# Revit family: 303_R401PX_+R460
name_source: partatom
category: Pipe Accessories
revit_build: Autodesk Revit 2018 (Build: 20170223_1515(x64)
units: mm (PartAtom-declared; Revit-internal decimal feet)

## family parameters
Always vertical = Yes
Cut with Voids When Loaded = No
Part Type = Valve - Breaks Into
Round Connector Dimension = Use Diameter
Shared = No
Work Plane-Based = No

## types (3) — shared parameters
CAT0 = Yes
CAT1 = No
Description = Angle valve with precision adjustment numberscale and protection cap
H4 = 2 mm  [stored 0.00656168 ft]
J1 = 6 mm  [stored 0.019685 ft]
J2 = 2 mm  [stored 0.00656168 ft]
J4 = 6 mm  [stored 0.019685 ft]
J5 = 6 mm  [stored 0.019685 ft]
L2D_Min = 3048 mm
M1 = 12 mm  [stored 0.0393701 ft]
M3 = 17 mm
M3__ve = -17 mm
Manufacturer = Giacomini
QmdConnectorList = 301;D;302;D1
TR1 = 15 mm  [stored 0.0492126 ft]
URL = http://www.giacomini.com
X1 = 17 mm
magiPartTypeId = 303
magiProductFamilyId = R401PX*+R460
zero-valued in all types: MC_Default_elevation

## per-type parameters (varying)
- R401PX032+R460: B1=6 mm  [stored 0.019685 ft]; B4=9 mm  [stored 0.0295276 ft]; CenSd_K1_6=10 mm  [stored 0.0328084 ft]; CenSd_W2_6=12 mm  [stored 0.0393701 ft]; D=10 mm; D1=10 mm; G1=5 mm  [stored 0.0164042 ft]; G3=7 mm  [stored 0.0229659 ft]; H3=4 mm  [stored 0.0131234 ft]; H3__ve=-4 mm; J=22 mm  [stored 0.0721785 ft]; K1=11 mm  [stored 0.0360892 ft]; KH=11 mm  [stored 0.0360892 ft]; KH__ve=-11 mm  [stored -0.0360892 ft]; L=40 mm  [stored 0.131234 ft]; L1=8 mm  [stored 0.0262467 ft]; L1__ve=-8 mm; L2D=40 mm  [stored 0.131234 ft]; LX=53 mm; R1=5 mm  [stored 0.0164042 ft]; TH2=78 mm; W1=11 mm  [stored 0.0360892 ft]; W2=14 mm  [stored 0.0459318 ft]; W2D=10 mm  [stored 0.0328084 ft]; X3=6 mm  [stored 0.019685 ft]; X4=4 mm  [stored 0.0131234 ft]; X41=3 mm  [stored 0.00984252 ft]; X41__ve=-3 mm; X4__ve=-4 mm
- R401PX034+R460: B1=8 mm  [stored 0.0262467 ft]; B4=14 mm  [stored 0.0459318 ft]; CenSd_K1_6=14 mm  [stored 0.0459318 ft]; CenSd_W2_6=16 mm; D=20 mm; D1=20 mm; G1=10 mm  [stored 0.0328084 ft]; G3=12 mm  [stored 0.0393701 ft]; H3=5 mm  [stored 0.0164042 ft]; H3__ve=-5 mm  [stored -0.0164042 ft]; J=25 mm  [stored 0.082021 ft]; K1=16 mm; KH=13 mm  [stored 0.0426509 ft]; KH__ve=-13 mm; L=46 mm; L1=10 mm  [stored 0.0328084 ft]; L1__ve=-10 mm  [stored -0.0328084 ft]; L2D=45 mm; LX=61 mm; R1=10 mm  [stored 0.0328084 ft]; TH2=77 mm; W1=15 mm  [stored 0.0492126 ft]; W2=19 mm; W2D=20 mm  [stored 0.0656168 ft]; X3=7 mm  [stored 0.0229659 ft]; X4=5 mm  [stored 0.0164042 ft]; X41=5 mm  [stored 0.0164042 ft]; X41__ve=-5 mm  [stored -0.0164042 ft]; X4__ve=-5 mm  [stored -0.0164042 ft]
- R401PX033+R460: B1=7 mm  [stored 0.0229659 ft]; B4=11 mm  [stored 0.0360892 ft]; CenSd_K1_6=12 mm  [stored 0.0393701 ft]; CenSd_W2_6=13 mm  [stored 0.0426509 ft]; D=15 mm; D1=15 mm; G1=7 mm  [stored 0.0229659 ft]; G3=9 mm  [stored 0.0295276 ft]; H3=5 mm  [stored 0.0164042 ft]; H3__ve=-5 mm  [stored -0.0164042 ft]; J=27 mm; K1=14 mm  [stored 0.0459318 ft]; KH=14 mm  [stored 0.0459318 ft]; KH__ve=-14 mm; L=43 mm; L1=9 mm  [stored 0.0295276 ft]; L1__ve=-9 mm; L2D=42 mm; LX=57 mm; R1=8 mm  [stored 0.0262467 ft]; TH2=77 mm; W1=12 mm  [stored 0.0393701 ft]; W2=15 mm  [stored 0.0492126 ft]; W2D=15 mm  [stored 0.0492126 ft]; X3=6 mm  [stored 0.019685 ft]; X4=4 mm  [stored 0.0131234 ft]; X41=4 mm  [stored 0.0131234 ft]; X41__ve=-4 mm; X4__ve=-4 mm

note: column(s) folded — value = type name in every type: magiProductCode, magiProductId

note: [stored X ft] marks values corroborated as IEEE doubles in the binary element streams (Revit-internal decimal feet)

## geometry (parser evidence)
native form markers: Sweep x1
no freeform markers — native parametric forms only
